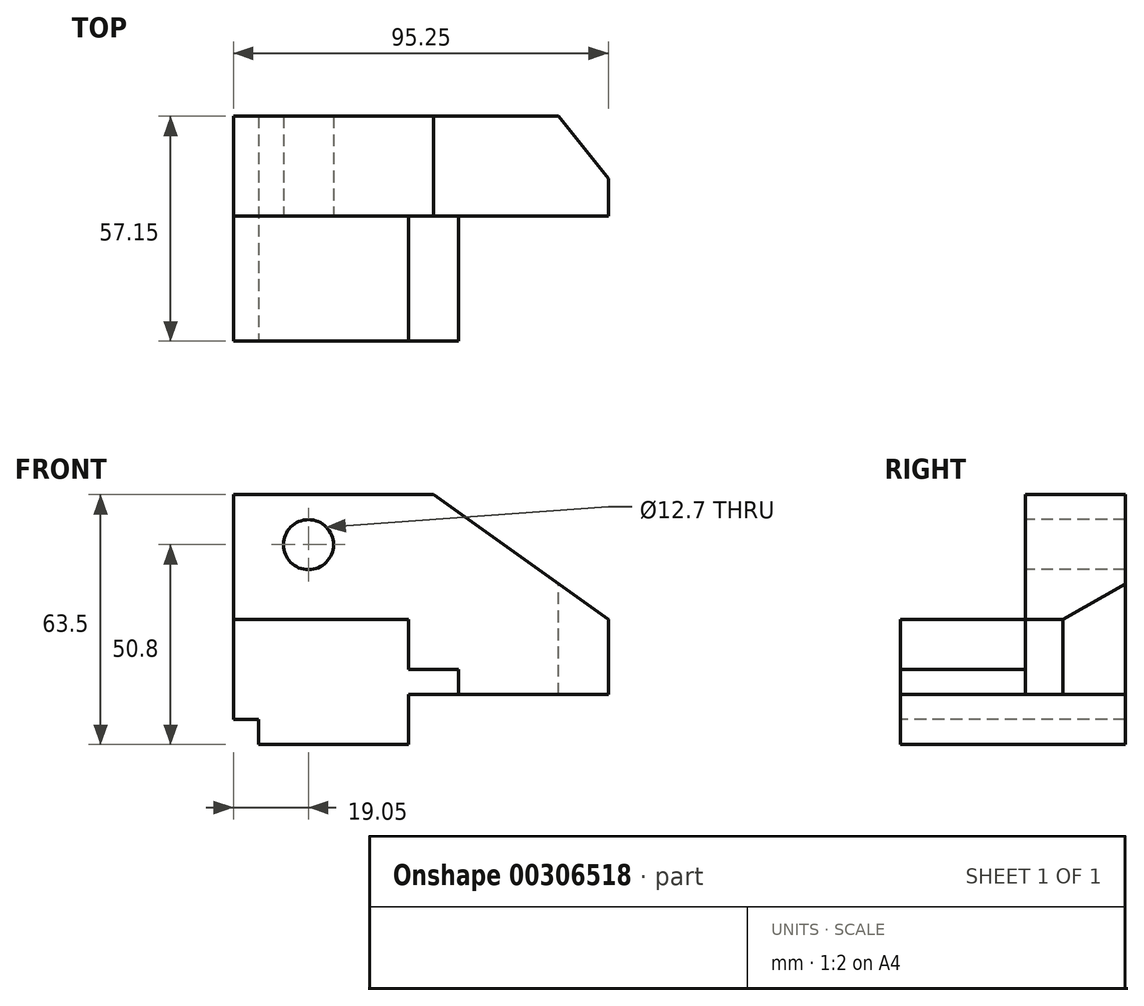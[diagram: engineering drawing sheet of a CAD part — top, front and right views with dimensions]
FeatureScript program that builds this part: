
annotation { "Feature Type Name" : "Feature", "Feature Type Description" : "" }
export const myFeature = defineFeature(function(context is Context, id is Id, definition is map)
    precondition{}
    {
        {
            var Q0;
            Q0=qCreatedBy(makeId("Right.planeOp"),FACE);
            var sketch = newSketch(context, id + "F0", { "sketchPlane" : qUnion([Q0])});
            skLineSegment(sketch, "E0.bottom", {"start": v(0, 0) * mm, "end": v(57.15, 0) * mm});
            skLineSegment(sketch, "E0.top", {"start": v(0, 63.5) * mm, "end": v(57.15, 63.5) * mm});
            skLineSegment(sketch, "E0.left", {"start": v(0, 0) * mm, "end": v(0, 63.5) * mm});
            skLineSegment(sketch, "E0.right", {"start": v(57.15, 0) * mm, "end": v(57.15, 63.5) * mm});
            skSolve(sketch);
        }
        {
            var Q0;
            Q0 = qSketchRegion(id + "F0", true);
            extrude(context, id + "F1", {"entities" : qUnion([Q0]), "depth" : 107.95 * mm});
        }
        {
            var Q0;
            Q0=makeQuery(id+"F1.opExtrude","SWEPT_FACE",FACE,{"disambiguationData":[OSD([sQuery(id+"F0.wireOp",EDGE,"E0.left")])]});
            var sketch = newSketch(context, id + "F2", { "sketchPlane" : qUnion([Q0])});
            skLineSegment(sketch, "E1.bottom", {"start": v(0, 0) * mm, "end": v(6.35, 0) * mm});
            skLineSegment(sketch, "E1.top", {"start": v(0, 6.35) * mm, "end": v(6.35, 6.35) * mm});
            skLineSegment(sketch, "E1.left", {"start": v(0, 0) * mm, "end": v(0, 6.35) * mm});
            skLineSegment(sketch, "E1.right", {"start": v(6.35, 0) * mm, "end": v(6.35, 6.35) * mm});
            skSolve(sketch);
        }
        {
            var Q0;
            Q0 = qSketchRegion(id + "F2", true);
            extrude(context, id + "F3", {"entities" : qUnion([Q0]), "operationType" : NewBodyOperationType.REMOVE, "endBound" : BoundingType.THROUGH_ALL, "oppositeDirection" : true, "depth" : 25.4 * mm});
        }
        {
            var Q0;
            Q0=makeQuery(id+"F1.opExtrude","SWEPT_FACE",FACE,{"disambiguationData":[OSD([sQuery(id+"F0.wireOp",EDGE,"E0.left")])]});
            var sketch = newSketch(context, id + "F4", { "sketchPlane" : qUnion([Q0])});
            skLineSegment(sketch, "E2.bottom", {"start": v(0, 31.75) * mm, "end": v(107.95, 31.75) * mm});
            skLineSegment(sketch, "E2.top", {"start": v(0, 63.5) * mm, "end": v(107.95, 63.5) * mm});
            skLineSegment(sketch, "E2.left", {"start": v(0, 31.75) * mm, "end": v(0, 63.5) * mm});
            skLineSegment(sketch, "E2.right", {"start": v(107.95, 31.75) * mm, "end": v(107.95, 63.5) * mm});
            skSolve(sketch);
        }
        {
            var Q0;
            Q0 = qSketchRegion(id + "F4", true);
            extrude(context, id + "F5", {"entities" : qUnion([Q0]), "operationType" : NewBodyOperationType.REMOVE, "oppositeDirection" : true, "depth" : 31.75 * mm});
        }
        {
            var Q0;
            Q0=makeQuery(id+"F1.opExtrude","SWEPT_FACE",FACE,{"disambiguationData":[OSD([sQuery(id+"F0.wireOp",EDGE,"E0.left")])]});
            var sketch = newSketch(context, id + "F6", { "sketchPlane" : qUnion([Q0])});
            skLineSegment(sketch, "E3.bottom", {"start": v(107.95, 31.75) * mm, "end": v(44.45, 31.75) * mm});
            skLineSegment(sketch, "E3.top", {"start": v(107.95, 19.05) * mm, "end": v(44.45, 19.05) * mm});
            skLineSegment(sketch, "E3.left", {"start": v(107.95, 31.75) * mm, "end": v(107.95, 19.05) * mm});
            skLineSegment(sketch, "E3.right", {"start": v(44.45, 31.75) * mm, "end": v(44.45, 19.05) * mm});
            skSolve(sketch);
        }
        {
            var Q0;
            Q0 = qSketchRegion(id + "F6", true);
            extrude(context, id + "F7", {"entities" : qUnion([Q0]), "operationType" : NewBodyOperationType.REMOVE, "oppositeDirection" : true, "depth" : 31.75 * mm});
        }
        {
            var Q0;
            Q0=makeQuery(id+"F1.opExtrude","SWEPT_FACE",FACE,{"disambiguationData":[OSD([sQuery(id+"F0.wireOp",EDGE,"E0.left")])]});
            var sketch = newSketch(context, id + "F8", { "sketchPlane" : qUnion([Q0])});
            skLineSegment(sketch, "E4.bottom", {"start": v(107.95, 0) * mm, "end": v(44.45, 0) * mm});
            skLineSegment(sketch, "E4.top", {"start": v(107.95, 12.7) * mm, "end": v(44.45, 12.7) * mm});
            skLineSegment(sketch, "E4.left", {"start": v(107.95, 0) * mm, "end": v(107.95, 12.7) * mm});
            skLineSegment(sketch, "E4.right", {"start": v(44.45, 0) * mm, "end": v(44.45, 12.7) * mm});
            skSolve(sketch);
        }
        {
            var Q0;
            Q0 = qSketchRegion(id + "F8", true);
            extrude(context, id + "F9", {"entities" : qUnion([Q0]), "operationType" : NewBodyOperationType.REMOVE, "endBound" : BoundingType.THROUGH_ALL, "oppositeDirection" : true, "depth" : 31.75 * mm});
        }
        {
            var Q0;
            Q0=makeQuery(id+"F1.opExtrude","SWEPT_FACE",FACE,{"disambiguationData":[OSD([sQuery(id+"F0.wireOp",EDGE,"E0.left")])]});
            var sketch = newSketch(context, id + "F10", { "sketchPlane" : qUnion([Q0])});
            skLineSegment(sketch, "E5.bottom", {"start": v(107.95, 12.7) * mm, "end": v(57.15, 12.7) * mm});
            skLineSegment(sketch, "E5.top", {"start": v(107.95, 19.05) * mm, "end": v(57.15, 19.05) * mm});
            skLineSegment(sketch, "E5.left", {"start": v(107.95, 12.7) * mm, "end": v(107.95, 19.05) * mm});
            skLineSegment(sketch, "E5.right", {"start": v(57.15, 12.7) * mm, "end": v(57.15, 19.05) * mm});
            skSolve(sketch);
        }
        {
            var Q0;
            Q0 = qSketchRegion(id + "F10", true);
            extrude(context, id + "F11", {"entities" : qUnion([Q0]), "operationType" : NewBodyOperationType.REMOVE, "oppositeDirection" : true, "depth" : 31.75 * mm});
        }
        {
            var Q0;
            Q0=makeQuery(id+"F11.boolean.opBoolean","MERGE",FACE,{"derivedFrom":[makeQuery(id+"F7.boolean.opBoolean","MERGE",FACE,{"derivedFrom":[makeQuery(id+"F5.boolean.opBoolean","COPY",FACE,{"derivedFrom":makeQuery(id+"F5.opExtrude","CAP_FACE",FACE,{"disambiguationData":[OSD([sQuery(id+"F4.wireOp",EDGE,"E2.bottom"),sQuery(id+"F4.wireOp",EDGE,"E2.top"),sQuery(id+"F4.wireOp",EDGE,"E2.left"),sQuery(id+"F4.wireOp",EDGE,"E2.right")])],"isStart":false})}),makeQuery(id+"F7.opExtrude","CAP_FACE",FACE,{"disambiguationData":[OSD([sQuery(id+"F6.wireOp",EDGE,"E3.bottom"),sQuery(id+"F6.wireOp",EDGE,"E3.top"),sQuery(id+"F6.wireOp",EDGE,"E3.left"),sQuery(id+"F6.wireOp",EDGE,"E3.right")])],"isStart":false})]}),makeQuery(id+"F11.opExtrude","CAP_FACE",FACE,{"disambiguationData":[OSD([sQuery(id+"F10.wireOp",EDGE,"E5.bottom"),sQuery(id+"F10.wireOp",EDGE,"E5.top"),sQuery(id+"F10.wireOp",EDGE,"E5.left"),sQuery(id+"F10.wireOp",EDGE,"E5.right")])],"isStart":false})]});
            var sketch = newSketch(context, id + "F12", { "sketchPlane" : qUnion([Q0])});
            skLineSegment(sketch, "E6.bottom", {"start": v(107.95, 12.7) * mm, "end": v(95.25, 12.7) * mm});
            skLineSegment(sketch, "E6.top", {"start": v(107.95, 63.5) * mm, "end": v(95.25, 63.5) * mm});
            skLineSegment(sketch, "E6.left", {"start": v(107.95, 12.7) * mm, "end": v(107.95, 63.5) * mm});
            skLineSegment(sketch, "E6.right", {"start": v(95.25, 12.7) * mm, "end": v(95.25, 63.5) * mm});
            skSolve(sketch);
        }
        {
            var Q0;
            Q0 = qSketchRegion(id + "F12", true);
            extrude(context, id + "F13", {"entities" : qUnion([Q0]), "operationType" : NewBodyOperationType.REMOVE, "endBound" : BoundingType.THROUGH_ALL, "oppositeDirection" : true, "depth" : 25.4 * mm});
        }
        {
            var Q0;
            Q0=makeQuery(id+"F1.opExtrude","SWEPT_FACE",FACE,{"disambiguationData":[OSD([sQuery(id+"F0.wireOp",EDGE,"E0.top")])]});
            var sketch = newSketch(context, id + "F14", { "sketchPlane" : qUnion([Q0])});
            skLineSegment(sketch, "E7", {"start": v(95.25, 41.27) * mm, "end": v(82.55, 57.15) * mm});
            skLineSegment(sketch, "E8", {"start": v(82.55, 57.15) * mm, "end": v(95.25, 57.15) * mm});
            skLineSegment(sketch, "E9", {"start": v(95.25, 57.15) * mm, "end": v(95.25, 41.27) * mm});
            skSolve(sketch);
        }
        {
            var Q0;
            Q0 = qSketchRegion(id + "F14", true);
            extrude(context, id + "F15", {"entities" : qUnion([Q0]), "operationType" : NewBodyOperationType.REMOVE, "endBound" : BoundingType.THROUGH_ALL, "oppositeDirection" : true, "depth" : 25.4 * mm});
        }
        {
            var Q0;
            Q0=makeQuery(id+"F11.boolean.opBoolean","MERGE",FACE,{"derivedFrom":[makeQuery(id+"F7.boolean.opBoolean","MERGE",FACE,{"derivedFrom":[makeQuery(id+"F5.boolean.opBoolean","COPY",FACE,{"derivedFrom":makeQuery(id+"F5.opExtrude","CAP_FACE",FACE,{"disambiguationData":[OSD([sQuery(id+"F4.wireOp",EDGE,"E2.bottom"),sQuery(id+"F4.wireOp",EDGE,"E2.top"),sQuery(id+"F4.wireOp",EDGE,"E2.left"),sQuery(id+"F4.wireOp",EDGE,"E2.right")])],"isStart":false})}),makeQuery(id+"F7.opExtrude","CAP_FACE",FACE,{"disambiguationData":[OSD([sQuery(id+"F6.wireOp",EDGE,"E3.bottom"),sQuery(id+"F6.wireOp",EDGE,"E3.top"),sQuery(id+"F6.wireOp",EDGE,"E3.left"),sQuery(id+"F6.wireOp",EDGE,"E3.right")])],"isStart":false})]}),makeQuery(id+"F11.opExtrude","CAP_FACE",FACE,{"disambiguationData":[OSD([sQuery(id+"F10.wireOp",EDGE,"E5.bottom"),sQuery(id+"F10.wireOp",EDGE,"E5.top"),sQuery(id+"F10.wireOp",EDGE,"E5.left"),sQuery(id+"F10.wireOp",EDGE,"E5.right")])],"isStart":false})]});
            var sketch = newSketch(context, id + "F16", { "sketchPlane" : qUnion([Q0])});
            skLineSegment(sketch, "E10", {"start": v(50.8, 63.5) * mm, "end": v(95.25, 31.75) * mm});
            skLineSegment(sketch, "E11", {"start": v(50.8, 63.5) * mm, "end": v(95.25, 63.5) * mm});
            skLineSegment(sketch, "E12", {"start": v(95.25, 63.5) * mm, "end": v(95.25, 31.75) * mm});
            skSolve(sketch);
        }
        {
            var Q0;
            Q0 = qSketchRegion(id + "F16", true);
            extrude(context, id + "F17", {"entities" : qUnion([Q0]), "operationType" : NewBodyOperationType.REMOVE, "endBound" : BoundingType.THROUGH_ALL, "oppositeDirection" : true, "depth" : 25.4 * mm});
        }
        {
            var Q0;
            Q0=makeQuery(id+"F11.boolean.opBoolean","MERGE",FACE,{"derivedFrom":[makeQuery(id+"F7.boolean.opBoolean","MERGE",FACE,{"derivedFrom":[makeQuery(id+"F5.boolean.opBoolean","COPY",FACE,{"derivedFrom":makeQuery(id+"F5.opExtrude","CAP_FACE",FACE,{"disambiguationData":[OSD([sQuery(id+"F4.wireOp",EDGE,"E2.bottom"),sQuery(id+"F4.wireOp",EDGE,"E2.top"),sQuery(id+"F4.wireOp",EDGE,"E2.left"),sQuery(id+"F4.wireOp",EDGE,"E2.right")])],"isStart":false})}),makeQuery(id+"F7.opExtrude","CAP_FACE",FACE,{"disambiguationData":[OSD([sQuery(id+"F6.wireOp",EDGE,"E3.bottom"),sQuery(id+"F6.wireOp",EDGE,"E3.top"),sQuery(id+"F6.wireOp",EDGE,"E3.left"),sQuery(id+"F6.wireOp",EDGE,"E3.right")])],"isStart":false})]}),makeQuery(id+"F11.opExtrude","CAP_FACE",FACE,{"disambiguationData":[OSD([sQuery(id+"F10.wireOp",EDGE,"E5.bottom"),sQuery(id+"F10.wireOp",EDGE,"E5.top"),sQuery(id+"F10.wireOp",EDGE,"E5.left"),sQuery(id+"F10.wireOp",EDGE,"E5.right")])],"isStart":false})]});
            var sketch = newSketch(context, id + "F18", { "sketchPlane" : qUnion([Q0])});
            skCircle(sketch, "E13", {"center": v(19.05, 50.8) * mm, "radius": 6.35 * mm});
            skSolve(sketch);
        }
        {
            var Q0;
            Q0 = qSketchRegion(id + "F18", true);
            extrude(context, id + "F19", {"entities" : qUnion([Q0]), "operationType" : NewBodyOperationType.REMOVE, "endBound" : BoundingType.THROUGH_ALL, "oppositeDirection" : true, "depth" : 25.4 * mm});
        }
    });
